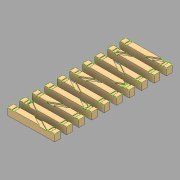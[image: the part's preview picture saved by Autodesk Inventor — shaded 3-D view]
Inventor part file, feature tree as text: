
AUTODESK INVENTOR PART (.ipt)
format: ipt  version: 2018 (Build 220112000, 112)  size: 436,736 bytes
history: native  units: mm
features: sketch x5, extrude x4
ambient origin geometry x8: Origin, YZ Plane, XZ Plane, XY Plane, X Axis, Y Axis, Z Axis, Center Point
bodies: Solid1 (feature_tree)
feature tree (9):
  sketch  "Sketch2"  dims[d0=300.0mm d1=0.0mm d2=25.0mm d3=0.0mm]
  extrude  "Extrusion1"  Depth=25.0mm TaperAngle=0.0deg
  extrude  "Extrusion2"  Depth=50.0mm TaperAngle=0.0deg
  extrude  "Extrusion3"  [1 undecoded]
  extrude  "Extrusion4"  [1 undecoded]
  sketch  "Sketch3"  dims[d4=25.0mm d5=0.0mm d6=50.0mm d7=0.0mm]
  sketch  "Sketch4"
  sketch  "Sketch5"
  sketch  "Sketch6"
note: 2 required parameter values undecoded (feature->parameter linkage not recoverable at this tier; creation-order binding heuristic only, values carry confidence <= 0.55)
